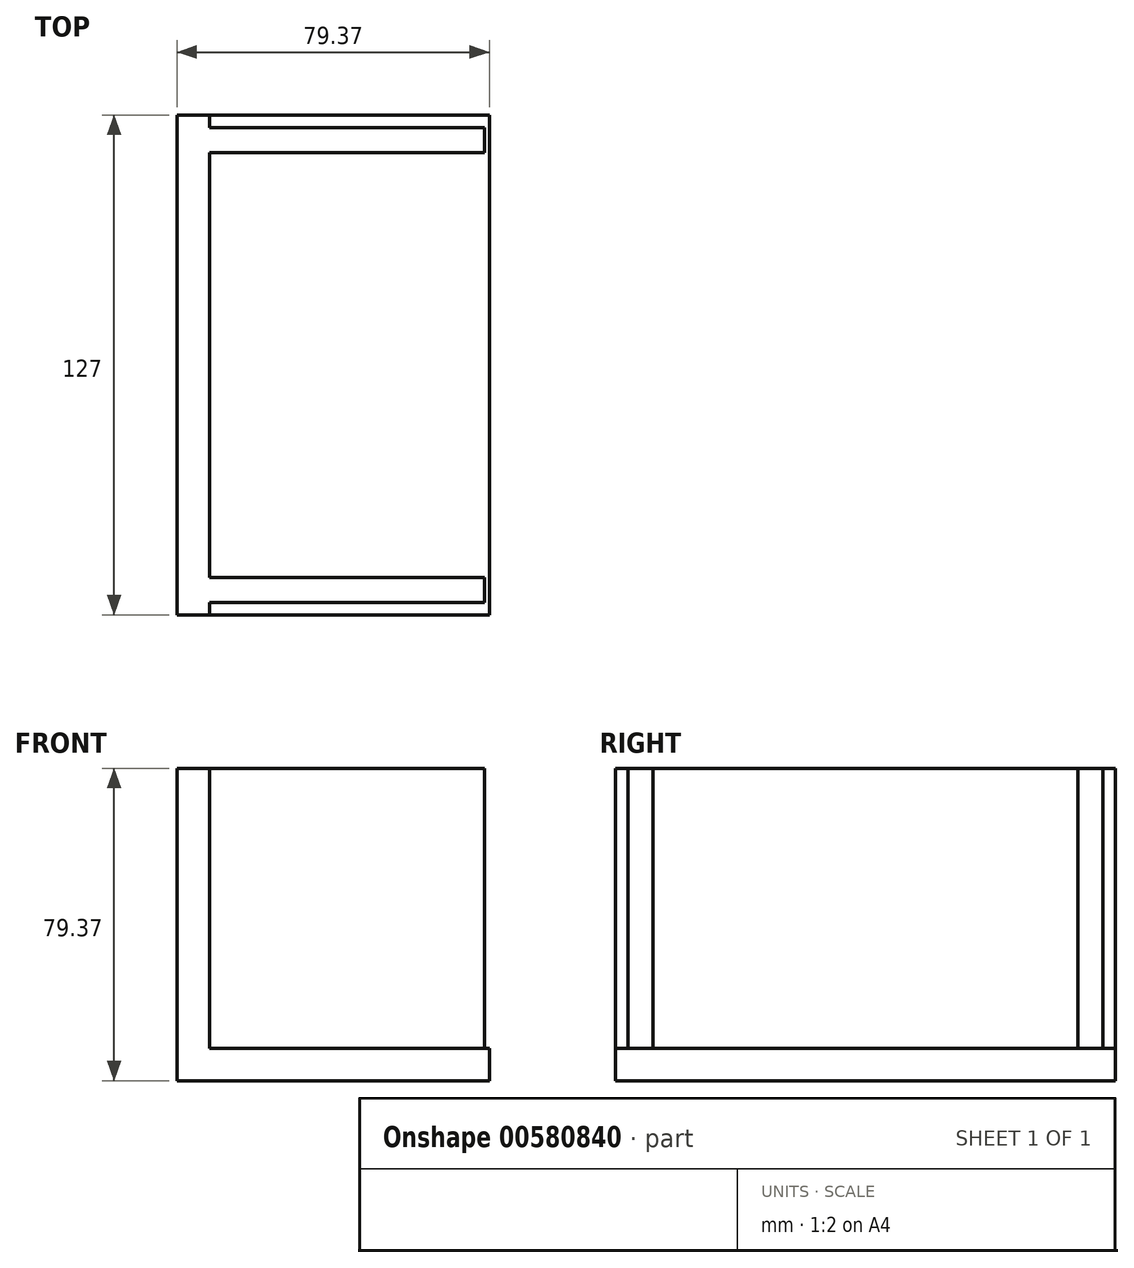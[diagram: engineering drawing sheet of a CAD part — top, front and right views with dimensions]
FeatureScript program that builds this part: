
annotation { "Feature Type Name" : "Feature", "Feature Type Description" : "" }
export const myFeature = defineFeature(function(context is Context, id is Id, definition is map)
    precondition{}
    {
        {
            var Q0;
            Q0=qCreatedBy(makeId("Front.planeOp"),FACE);
            var sketch = newSketch(context, id + "F0", { "sketchPlane" : qUnion([Q0])});
            skLineSegment(sketch, "E0.bottom", {"start": v(-51.75, 38.88) * mm, "end": v(-43.5, 38.88) * mm});
            skLineSegment(sketch, "E0.top", {"start": v(-51.75, -40.5) * mm, "end": v(27.62, -40.5) * mm});
            skLineSegment(sketch, "E0.left", {"start": v(-51.75, 38.88) * mm, "end": v(-51.75, -40.5) * mm});
            skLineSegment(sketch, "E0.right", {"start": v(27.62, -32.24) * mm, "end": v(27.62, -40.5) * mm});
            skLineSegment(sketch, "E1.top", {"start": v(27.62, -32.24) * mm, "end": v(-43.5, -32.24) * mm});
            skLineSegment(sketch, "E1.right", {"start": v(-43.5, 38.88) * mm, "end": v(-43.5, -32.24) * mm});
            skSolve(sketch);
        }
        {
            var Q0;
            Q0 = qSketchRegion(id + "F0", true);
            extrude(context, id + "F1", {"entities" : qUnion([Q0]), "depth" : 127 * mm, "offsetDistance" : 25.4 * mm});
        }
        {
            var Q0;
            Q0=makeQuery(id+"F1.opExtrude","SWEPT_FACE",FACE,{"disambiguationData":[OSD([sQuery(id+"F0.wireOp",EDGE,"E1.right")])]});
            var sketch = newSketch(context, id + "F2", { "sketchPlane" : qUnion([Q0])});
            skLineSegment(sketch, "E2.bottom", {"start": v(-123.83, 38.88) * mm, "end": v(-117.48, 38.88) * mm});
            skLineSegment(sketch, "E2.top", {"start": v(-123.83, -32.24) * mm, "end": v(-117.48, -32.24) * mm});
            skLineSegment(sketch, "E2.left", {"start": v(-123.83, 38.88) * mm, "end": v(-123.83, -32.24) * mm});
            skLineSegment(sketch, "E2.right", {"start": v(-117.48, 38.88) * mm, "end": v(-117.48, -32.24) * mm});
            skLineSegment(sketch, "E3.bottom", {"start": v(-9.52, 38.88) * mm, "end": v(-3.18, 38.88) * mm});
            skLineSegment(sketch, "E3.top", {"start": v(-9.52, -32.24) * mm, "end": v(-3.17, -32.24) * mm});
            skLineSegment(sketch, "E3.left", {"start": v(-9.53, 38.88) * mm, "end": v(-9.52, -32.24) * mm});
            skLineSegment(sketch, "E3.right", {"start": v(-3.18, 38.88) * mm, "end": v(-3.17, -32.24) * mm});
            skSolve(sketch);
        }
        {
            var Q0;
            Q0 = qSketchRegion(id + "F2", true);
            extrude(context, id + "F3", {"entities" : qUnion([Q0]), "operationType" : NewBodyOperationType.ADD, "depth" : 69.85 * mm, "offsetDistance" : 25.4 * mm});
        }
    });
